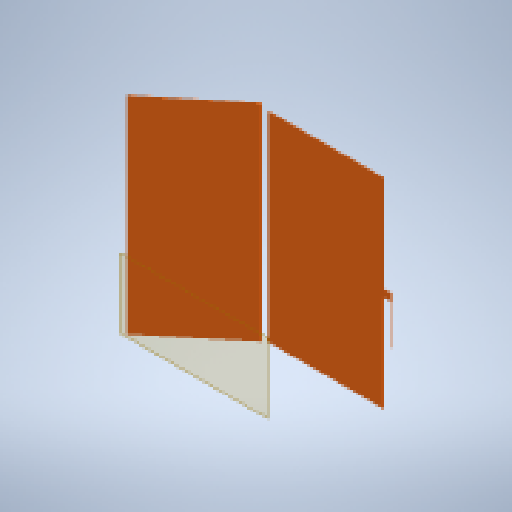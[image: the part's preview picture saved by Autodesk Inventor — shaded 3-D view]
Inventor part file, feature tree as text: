
AUTODESK INVENTOR PART (.ipt)
format: ipt  version: 2025 (Build 290162000, 162)  size: 163,840 bytes
history: native  units: in
note: dims shown in document units (in); Inventor stores cm internally (conversion verified against a paired STEP export)
features: reference x18, other x18, plane x1, extrude x1, sketch x1
ambient origin geometry x8: Origin, YZ Plane, XZ Plane, XY Plane, X Axis, Y Axis, Z Axis, Center Point
bodies: Solid1 (feature_tree)
feature tree (39):
  plane  "Work Plane1"
  extrude  "Extrusion1"  [1 undecoded]
  sketch  "Sketch1"  dims[d0=0.25in d1=0.0in]
  reference  "Reference1"
  reference  "Reference2"
  reference  "Reference3"
  reference  "Reference4"
  reference  "Reference5"
  reference  "Reference6"
  reference  "Reference7"
  reference  "Reference8"
  reference  "Reference9"
  reference  "Reference10"
  reference  "Reference11"
  reference  "Reference12"
  reference  "Reference13"
  reference  "Reference14"
  reference  "Reference15"
  reference  "Reference16"
  reference  "Reference17"
  reference  "Reference18"
  other  "<userpath>\Documents\GitHub\USCTigerBurn24\v2\Tiger.iam"
  other  "Tiger.iam"
  other  "back slant:4"
  other  "2X4X92:1"
  other  "2X4X65.191:4"
  other  "back slant:1"
  other  "2x4x120:6"
  other  "2x4x120:4"
  other  "4x4x66:7"
  other  "4x4x55:2"
  other  "4x4x55:1"
  other  "4x4x66:1"
  other  "4x4x96:13"
  other  "4x4x66:3"
  other  "2x4x76:5"
  other  "2x4x36:36"
  other  "2x4x24:18"
  other  "4x4x66:5"
note: 1 required parameter value undecoded (feature->parameter linkage not recoverable at this tier; creation-order binding heuristic only, values carry confidence <= 0.55)
